# Revit family: Bticino universal columns
name_source: partatom
category: Installations électriques
units: mm (PartAtom-declared; Revit-internal decimal feet)

## family parameters
Basée sur le plan de construction = Non
Conserver l'orientation des annotations = Non
Cote de connecteur circulaire = Utiliser le diamètre
Couper avec des vides une fois chargée = Non
Partagée = Non
Point de calcul de pièce = Non
Toujours verticalement = Oui
Type d'élément = Normal

## types (8) — shared parameters
Fabricant = BTCINO
Largeur = 75 mm
Main Material = Aluminum
Standard = Universal
Séparateur = 35 mm
zero-valued in all types: Elévation par défaut

## per-type parameters (varying)
| type | 1 CPT | 2 CPT | Description | Finishing | H1 | HC | L2 | Longueur | Matériau couvercle | Matériaux corps | Modèle | Number of compartments | Ovaline_kit |
| IDS_129201NBA | Oui | Non | IDS_DESCRITPION_129201NBA | White | 2700 mm  [stored 8.85827 ft] | 2660 mm  [stored 8.72703 ft] | 150 mm | 82 mm | Legrand - Plastique blanc | Legrand - Aluminium blanc | 129201NBA | 1 compartment | Non |
| IDS_129201NAL | Oui | Non | IDS_DESCRITPION_129201NAL | Aluminum | 2700 mm  [stored 8.85827 ft] | 2660 mm  [stored 8.72703 ft] | 150 mm | 82 mm | Legrand - Plastique gris | Legrand - Aluminium gris | 129201NAL | 1 compartment | Non |
| IDS_129201NNR | Oui | Non | IDS_DESCRITPION_129201NNR | Black | 2700 mm  [stored 8.85827 ft] | 2660 mm  [stored 8.72703 ft] | 150 mm | 82 mm | Legrand - Plastique noir | Legrand - Aluminium noir | 129201NNR | 1 compartment | Non |
| IDS_129001NBA | Non | Oui | IDS_DESCRITPION_129001NBA | White | 2700 mm  [stored 8.85827 ft] | 2660 mm  [stored 8.72703 ft] | 150 mm | 125 mm | Legrand - Plastique blanc | Legrand - Aluminium blanc | 129001NBA | 2 compartments | Non |
| IDS_129001NAL | Non | Oui | IDS_DESCRITPION_129001NAL | Aluminum | 2700 mm  [stored 8.85827 ft] | 2660 mm  [stored 8.72703 ft] | 150 mm | 125 mm | Legrand - Plastique gris | Legrand - Aluminium gris | 129001NAL | 2 compartments | Non |
| IDS_129001NNR | Non | Oui | IDS_DESCRITPION_129001NNR | Black | 2700 mm  [stored 8.85827 ft] | 2660 mm  [stored 8.72703 ft] | 150 mm | 125 mm | Legrand - Plastique noir | Legrand - Aluminium noir | 129001NNR | 2 compartments | Non |
| IDS_129202NAL | Oui | Non | IDS_DESCRITPION_129202NAL | Aluminum | 2700 mm  [stored 8.85827 ft] | 2660 mm  [stored 8.72703 ft] | 150 mm | 82 mm | Legrand - Plastique gris | Legrand - Aluminium gris | 129202NAL | 1 compartment | Non |
| IDS_129304NAL | Oui | Non | IDS_DESCRITPION_129304NAL | Aluminum | 680 mm  [stored 2.23097 ft] | 640 mm  [stored 2.09974 ft] | 2720 mm  [stored 8.92388 ft] | 82 mm | Legrand - Plastique gris | Legrand - Aluminium gris | 129304NAL | 1 compartment | Oui |

note: [stored X ft] marks values corroborated as IEEE doubles in the binary element streams (Revit-internal decimal feet)
